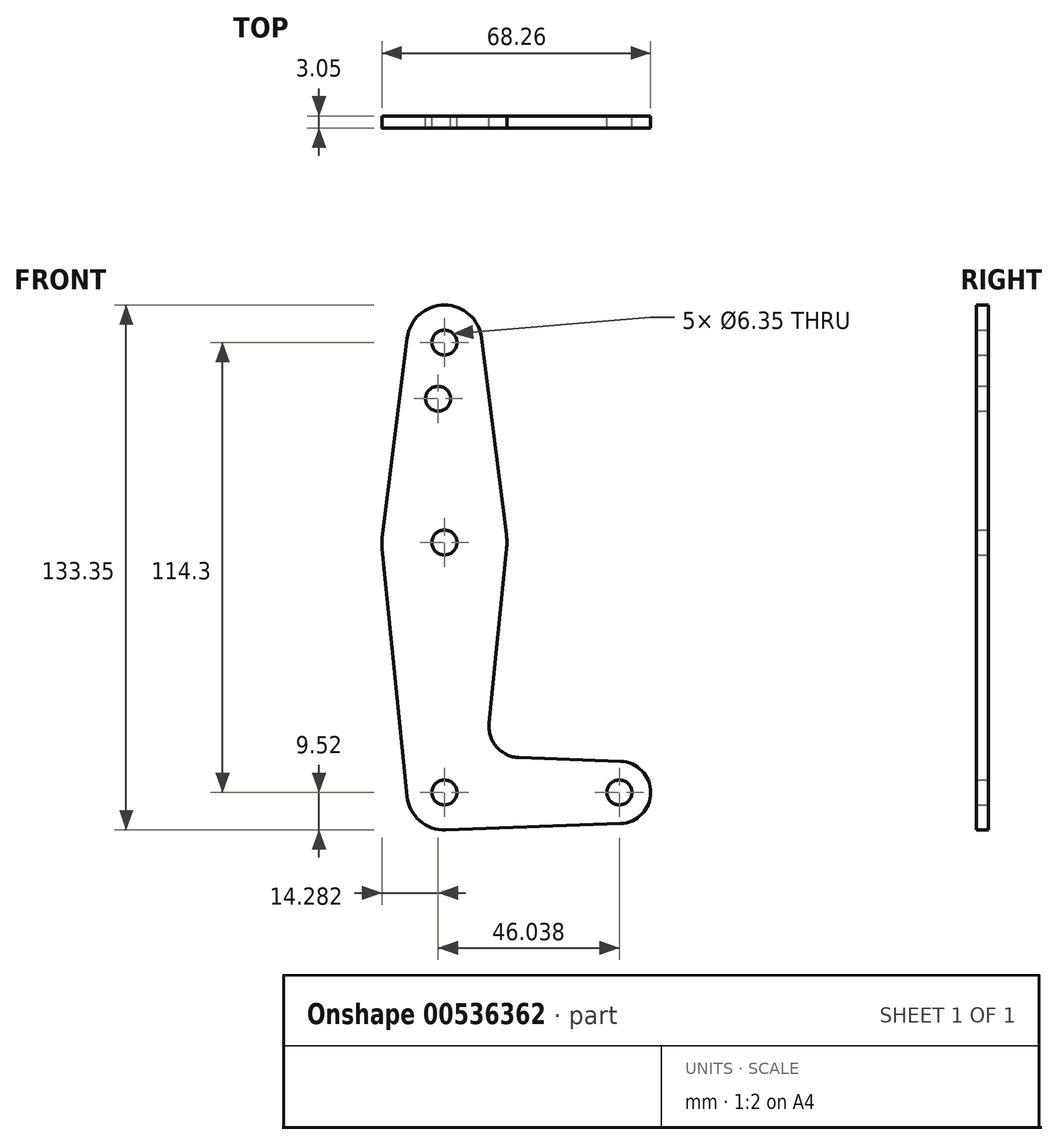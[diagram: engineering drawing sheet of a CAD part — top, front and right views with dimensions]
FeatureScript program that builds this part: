
annotation { "Feature Type Name" : "Feature", "Feature Type Description" : "" }
export const myFeature = defineFeature(function(context is Context, id is Id, definition is map)
    precondition{}
    {
        {
            var Q0;
            Q0=qCreatedBy(makeId("Front.planeOp"),FACE);
            var sketch = newSketch(context, id + "F0", { "sketchPlane" : qUnion([Q0])});
            skLineSegment(sketch, "E0", {"start": v(0, 0) * mm, "end": v(0, 63.5) * mm, "construction": true});
            skLineSegment(sketch, "E1.bottom", {"start": v(0, 0) * mm, "end": v(44.45, 0) * mm});
            skLineSegment(sketch, "E1.top", {"start": v(0, 0) * mm, "end": v(44.45, 0) * mm});
            skLineSegment(sketch, "E1.left", {"start": v(0, 0) * mm, "end": v(0, 0) * mm});
            skLineSegment(sketch, "E1.right", {"start": v(44.45, 0) * mm, "end": v(44.45, 0) * mm});
            skCircle(sketch, "E2", {"center": v(0, 114.3) * mm, "radius": 9.53 * mm});
            skCircle(sketch, "E3", {"center": v(0, 0) * mm, "radius": 9.53 * mm});
            skLineSegment(sketch, "E4", {"start": v(0, 0) * mm, "end": v(0, 114.3) * mm, "construction": true});
            skCircle(sketch, "E5", {"center": v(0, 63.5) * mm, "radius": 15.88 * mm});
            skCircle(sketch, "E6", {"center": v(44.45, 0) * mm, "radius": 7.94 * mm});
            skLineSegment(sketch, "E7", {"start": v(-9.45, 115.5) * mm, "end": v(-15.75, 65.48) * mm});
            skLineSegment(sketch, "E8", {"start": v(9.45, 115.5) * mm, "end": v(15.75, 65.48) * mm});
            skLineSegment(sketch, "E9", {"start": v(-15.8, 61.91) * mm, "end": v(-9.48, -0.95) * mm});
            skLineSegment(sketch, "E10", {"start": v(15.8, 61.91) * mm, "end": v(11.34, 17.6) * mm});
            skLineSegment(sketch, "E11", {"start": v(0.34, -9.52) * mm, "end": v(44.73, -7.93) * mm});
            skLineSegment(sketch, "E12", {"start": v(18.97, 8.85) * mm, "end": v(44.73, 7.93) * mm});
            skCircle(sketch, "E13", {"center": v(0, 114.3) * mm, "radius": 3.18 * mm});
            skCircle(sketch, "E14", {"center": v(0, 63.5) * mm, "radius": 3.18 * mm});
            skCircle(sketch, "E15", {"center": v(0, 0) * mm, "radius": 3.18 * mm});
            skCircle(sketch, "E16", {"center": v(44.45, 0) * mm, "radius": 3.18 * mm});
            skCircle(sketch, "E17", {"center": v(-1.59, 100.03) * mm, "radius": 3.18 * mm});
            skArc(sketch, "E18.filletArc", {"start": v(11.34, 17.6) * mm, "mid": v(13.26, 11.57) * mm, "end": v(18.97, 8.85) * mm});
            skSolve(sketch);
        }
        {
            var Q0;
            Q0 = qSketchRegion(id + "F0", true);
            extrude(context, id + "F1", {"entities" : qUnion([Q0]), "depth" : 3.05 * mm, "offsetDistance" : 25.4 * mm});
        }
    });
